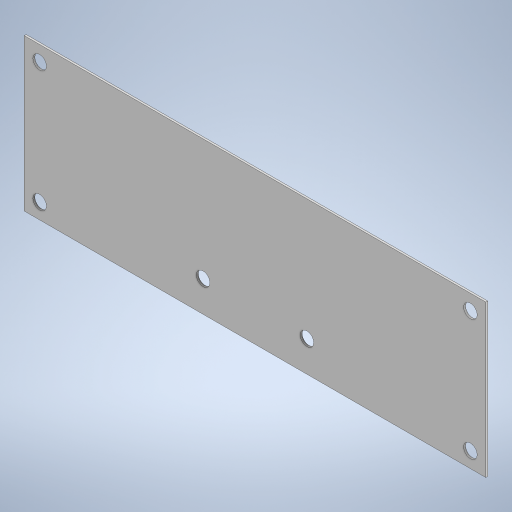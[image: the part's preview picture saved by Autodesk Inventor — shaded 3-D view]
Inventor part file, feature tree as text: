
AUTODESK INVENTOR PART (.ipt)
format: ipt  version: 2023 (Build 270158000, 158)  size: 233,472 bytes
history: native  units: mm
features: extrude x3, sketch x3
ambient origin geometry x8: Origin, YZ Plane, XZ Plane, XY Plane, X Axis, Y Axis, Z Axis, Center Point
bodies: Body1 (feature_tree)
feature tree (6):
  extrude  "Extrusion45"  Depth=79.0mm
  extrude  "Extrusion47"  Depth=1.0mm
  extrude  "Extrusion48"  Depth=7.0mm
  sketch  "Sketch66"  dims[d179=240.0mm d180=79.0mm]
  sketch  "Sketch68"  dims[d181=1.0mm d182=0.0mm d186=7.0mm]
  sketch  "Sketch69"  dims[d187=7.0mm d188=7.0mm d189=7.0mm d190=0.0mm d191=0.0mm d192=7.0mm d193=7.0mm d194=0.0mm d195=0.0mm d49=0.5mm d50=0.872665mm d51=0.5mm d52=0.872665mm d130=0.5mm d131=0.872665mm d132=0.5mm d133=0.872665mm d156=0.5mm d157=0.872665mm d158=0.5mm d159=0.872665mm]
